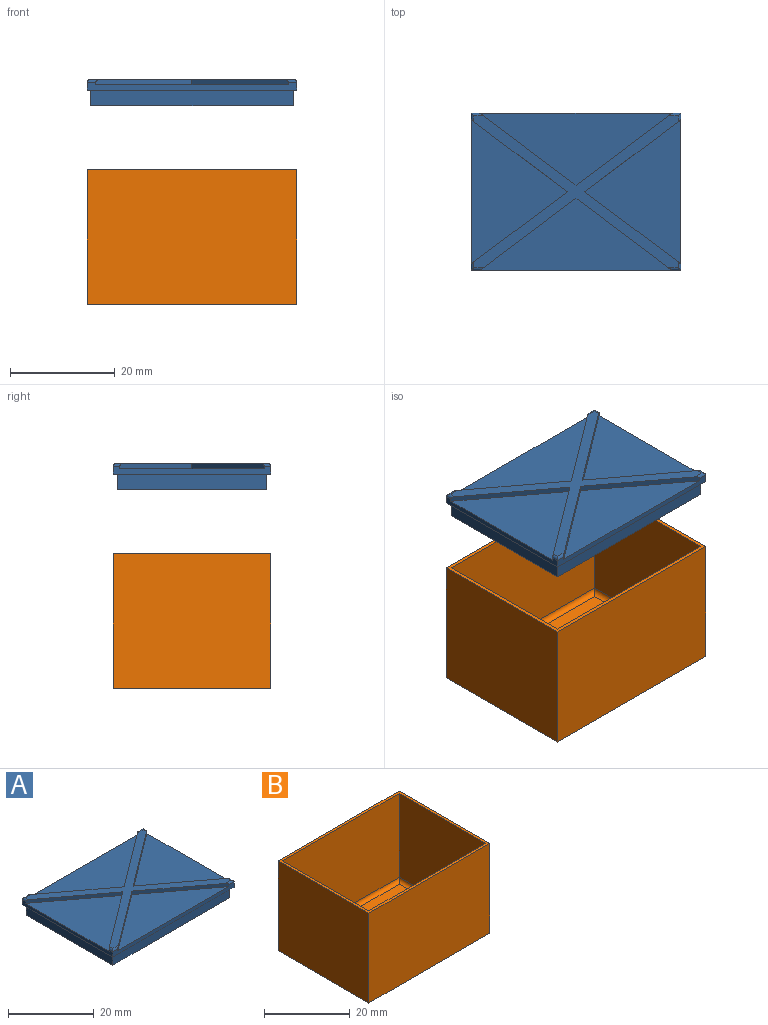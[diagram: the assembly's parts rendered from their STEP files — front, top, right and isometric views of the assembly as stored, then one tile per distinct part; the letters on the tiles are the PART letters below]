
ASSEMBLY  parts=2 mates=1
PART A: 40 faces, bbox 40x30x5 mm
  f0: plane 27.5x18.33mm, normal (0,0,1), area 252.1mm2, adj f16,f29,f30
  f1: plane 36.67x13.75mm, normal (0,0,1), area 252.1mm2, adj f17,f27,f28
  f2: plane 27.5x18.33mm, normal (0,0,1), area 252.1mm2, adj f14,f25,f26
  f3: plane 36.67x13.75mm, normal (0,0,1), area 252.1mm2, adj f15,f23,f24
  f4: plane 38.6x3mm, normal (0,-1,0), area 115.8mm2, adj f5,f11,f12,f13
  f5: plane 28.6x3mm, normal (1,0,0), area 85.8mm2, adj f4,f6,f12,f13
  f6: plane 38.6x3mm, normal (0,1,0), area 115.8mm2, adj f5,f11,f12,f13
  f7: plane 27.2x2mm, normal (-1,0,0), area 54.4mm2, adj f8,f10,f12,f20
  f8: plane 37.2x2mm, normal (0,1,0), area 74.4mm2, adj f7,f9,f12,f19
  f9: plane 27.2x2mm, normal (1,0,0), area 54.4mm2, adj f8,f10,f12,f21
  f10: plane 37.2x2mm, normal (0,-1,0), area 74.4mm2, adj f7,f9,f12,f22
  f11: plane 28.6x3mm, normal (-1,0,0), area 85.8mm2, adj f4,f6,f12,f13
  f12: plane 38.6x28.6mm, normal (0,0,-1), area 92.1mm2, adj f4,f5,f6,f7,f8,f9,f10,f11
  f13: plane 40x30mm, normal (0,0,-1), area 96mm2, adj f4,f5,f6,f11,f14,f15,f16,f17
  f14: plane 30x1.5mm, normal (-1,0,0), area 31.3mm2, adj f2,f13,f15,f17,f25,f26,f32,f34
  f15: plane 40x1.5mm, normal (0,1,0), area 41.7mm2, adj f3,f13,f14,f16,f23,f24,f35,f36
  f16: plane 30x1.5mm, normal (1,0,0), area 31.3mm2, adj f0,f13,f15,f17,f29,f30,f37,f38
  f17: plane 40x1.5mm, normal (0,-1,0), area 41.7mm2, adj f1,f13,f14,f16,f27,f28,f33,f39
  f18: plane 35.2x25.2mm, normal (0,0,-1), area 887mm2, adj f19,f20,f21,f22
  f19: cylinder r=1mm len=37.2mm, axis (-1,0,0), area 57.3mm2, adj f8,f18,f20,f21
  f20: cylinder r=1mm len=27.2mm, axis (0,-1,0), area 41.6mm2, adj f7,f18,f19,f22
  f21: cylinder r=1mm len=27.2mm, axis (0,1,0), area 41.6mm2, adj f9,f18,f19,f22
  f22: cylinder r=1mm len=37.2mm, axis (1,0,0), area 57.3mm2, adj f10,f18,f20,f21
  f23: plane 18.33x13.75mm, normal (-0.6,0.8,0), area 22.8mm2, adj f3,f15,f24,f31,f36
  f24: plane 18.33x13.75mm, normal (0.6,0.8,0), area 22.8mm2, adj f3,f15,f23,f31,f35
  f25: plane 18.33x13.75mm, normal (-0.6,-0.8,0), area 22.8mm2, adj f2,f14,f26,f31,f34
  f26: plane 18.33x13.75mm, normal (-0.6,0.8,0), area 22.8mm2, adj f2,f14,f25,f31,f32
  f27: plane 18.33x13.75mm, normal (0.6,-0.8,0), area 22.8mm2, adj f1,f17,f28,f31,f33
  f28: plane 18.33x13.75mm, normal (-0.6,-0.8,0), area 22.8mm2, adj f1,f17,f27,f31,f39
  f29: plane 18.33x13.75mm, normal (0.6,0.8,0), area 22.8mm2, adj f0,f16,f30,f31,f38
  f30: plane 18.33x13.75mm, normal (0.6,-0.8,0), area 22.8mm2, adj f0,f16,f29,f31,f37
  f31: plane 39x29mm, normal (0,0,1), area 185.8mm2, adj f23,f24,f25,f26,f27,f28,f29,f30
  f32: cylinder r=0.5mm len=1.63mm, axis (0,1,0), area 0.9mm2, adj f14,f26,f31,f33
  f33: cylinder r=0.5mm len=2.33mm, axis (-1,0,0), area 1.4mm2, adj f17,f27,f31,f32
  f34: cylinder r=0.5mm len=1.63mm, axis (0,1,0), area 0.9mm2, adj f14,f25,f31,f35
  f35: cylinder r=0.5mm len=2.33mm, axis (1,0,0), area 1.4mm2, adj f15,f24,f31,f34
  f36: cylinder r=0.5mm len=2.33mm, axis (1,0,0), area 1.4mm2, adj f15,f23,f31,f37
  f37: cylinder r=0.5mm len=1.63mm, axis (0,-1,0), area 0.9mm2, adj f16,f30,f31,f36
  f38: cylinder r=0.5mm len=1.63mm, axis (0,-1,0), area 0.9mm2, adj f16,f29,f31,f39
  f39: cylinder r=0.5mm len=2.33mm, axis (-1,0,0), area 1.4mm2, adj f17,f28,f31,f38
PART B: 15 faces, bbox 40x30x25.7 mm
  f0: plane 40x25.7mm, normal (0,-1,0), area 1028mm2, adj f1,f3,f4,f9
  f1: plane 30x25.7mm, normal (1,0,0), area 771mm2, adj f0,f2,f4,f9
  f2: plane 40x25.7mm, normal (0,1,0), area 1028mm2, adj f1,f3,f4,f9
  f3: plane 30x25.7mm, normal (-1,0,0), area 771mm2, adj f0,f2,f4,f9
  f4: plane 40x30mm, normal (0,0,-1), area 1200mm2, adj f0,f1,f2,f3
  f5: plane 28.6x24mm, normal (-1,0,0), area 686.4mm2, adj f6,f8,f9,f12
  f6: plane 38.6x24mm, normal (0,1,0), area 926.4mm2, adj f5,f7,f9,f11
  f7: plane 28.6x24mm, normal (1,0,0), area 686.4mm2, adj f6,f8,f9,f13
  f8: plane 38.6x24mm, normal (0,-1,0), area 926.4mm2, adj f5,f7,f9,f14
  f9: plane 40x30mm, normal (0,0,1), area 96mm2, adj f0,f1,f2,f3,f5,f6,f7,f8
  f10: plane 36.6x26.6mm, normal (0,0,1), area 973.6mm2, adj f11,f12,f13,f14
  f11: cylinder r=1mm len=38.6mm, axis (-1,0,0), area 59.5mm2, adj f6,f10,f12,f13
  f12: cylinder r=1mm len=28.6mm, axis (0,-1,0), area 43.8mm2, adj f5,f10,f11,f14
  f13: cylinder r=1mm len=28.6mm, axis (0,1,0), area 43.8mm2, adj f7,f10,f11,f14
  f14: cylinder r=1mm len=38.6mm, axis (1,0,0), area 59.5mm2, adj f8,f10,f12,f13
PLACE A t=(12.56,6.57,6.3)mm
PLACE B t=(12.56,6.57,-8.86)mm
MATE slider A.f13 <-> B.f9  axis (0,0,1) through (-6.74,20.87,32)mm
